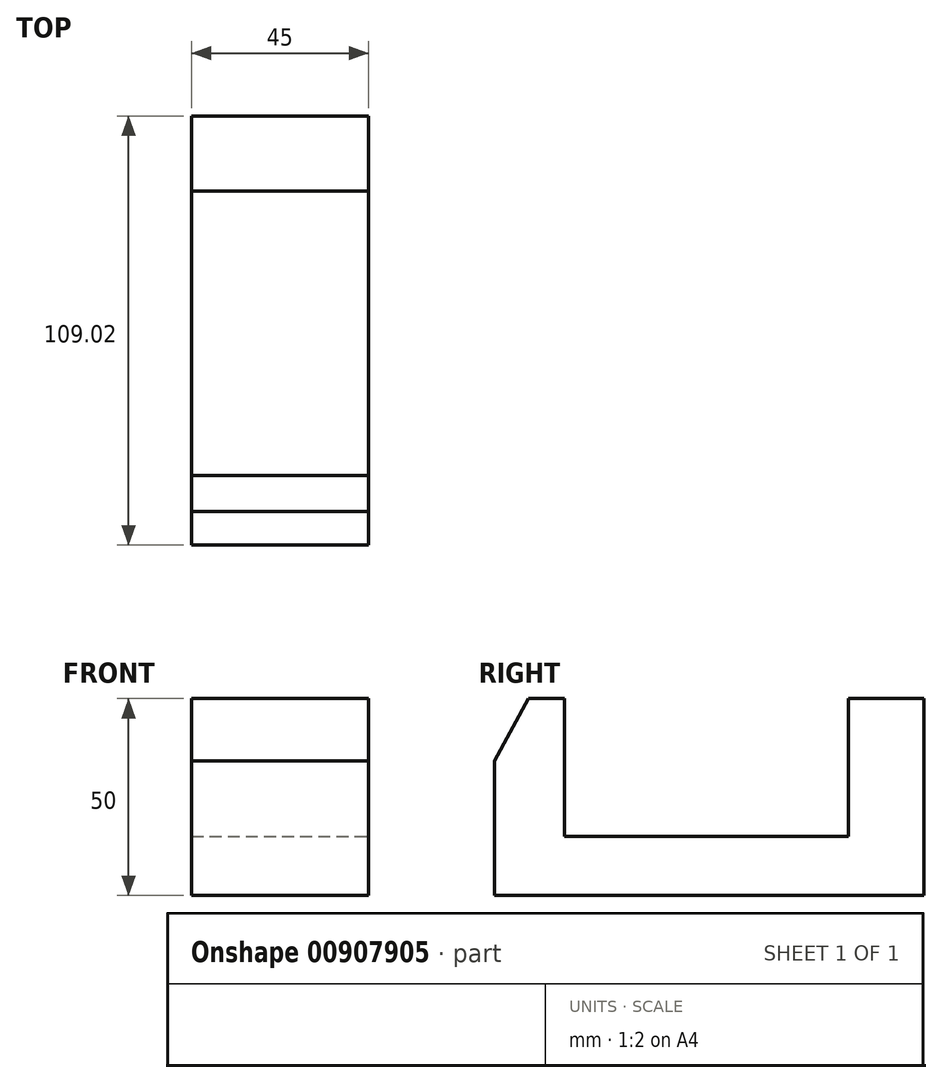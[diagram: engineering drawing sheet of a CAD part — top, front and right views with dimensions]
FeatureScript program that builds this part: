
annotation { "Feature Type Name" : "Feature", "Feature Type Description" : "" }
export const myFeature = defineFeature(function(context is Context, id is Id, definition is map)
    precondition{}
    {
        {
            var Q0;
            Q0=qCreatedBy(makeId("Right.planeOp"),FACE);
            var sketch = newSketch(context, id + "F0", { "sketchPlane" : qUnion([Q0])});
            skLineSegment(sketch, "E0", {"start": v(-51.67, -34.17) * mm, "end": v(57.35, -34.17) * mm});
            skLineSegment(sketch, "E1", {"start": v(-51.67, -34.17) * mm, "end": v(-51.67, 15.83) * mm});
            skLineSegment(sketch, "E2", {"start": v(57.35, -34.17) * mm, "end": v(57.35, 15.83) * mm});
            skLineSegment(sketch, "E3", {"start": v(57.35, 15.83) * mm, "end": v(-51.67, 15.83) * mm});
            skSolve(sketch);
        }
        {
            var Q0;
            Q0=makeQuery(id+"F0.imprint","IMPRINT",FACE,{"disambiguationData":[TD([[makeQuery(id+"F0.imprint","IMPRINT",EDGE,{"derivedFrom":sQuery(id+"F0.wireOp",EDGE,"E0")}),1.0]])]});
            extrude(context, id + "F1", {"entities" : qUnion([Q0]), "depth" : 45 * mm, "offsetDistance" : 25 * mm});
        }
        {
            var Q0;
            Q0=makeQuery(id+"F1.opExtrude","CAP_FACE",FACE,{"disambiguationData":[OSD([sQuery(id+"F0.wireOp",EDGE,"E0"),sQuery(id+"F0.wireOp",EDGE,"E1"),sQuery(id+"F0.wireOp",EDGE,"E2"),sQuery(id+"F0.wireOp",EDGE,"E3")])],"isStart":false});
            var sketch = newSketch(context, id + "F2", { "sketchPlane" : qUnion([Q0])});
            skLineSegment(sketch, "E4", {"start": v(-43.1, 15.83) * mm, "end": v(-51.67, 0) * mm});
            skSolve(sketch);
        }
        {
            var Q0;
            {var subQ0=sQuery(id+"F2.wireOp",EDGE,"E4");Q0=makeQuery(id+"F2.imprint","IMPRINT",FACE,{"disambiguationData":[TD([[makeQuery(id+"F2.imprint","IMPRINT",EDGE,{"derivedFrom":subQ0}),-1.0]])]});}
            extrude(context, id + "F3", {"entities" : qUnion([Q0]), "operationType" : NewBodyOperationType.REMOVE, "oppositeDirection" : true, "depth" : 207 * mm, "offsetDistance" : 25 * mm});
        }
        {
            var Q0;
            Q0=makeQuery(id+"F1.opExtrude","CAP_FACE",FACE,{"disambiguationData":[OSD([sQuery(id+"F0.wireOp",EDGE,"E0"),sQuery(id+"F0.wireOp",EDGE,"E1"),sQuery(id+"F0.wireOp",EDGE,"E2"),sQuery(id+"F0.wireOp",EDGE,"E3")])],"isStart":false});
            var sketch = newSketch(context, id + "F4", { "sketchPlane" : qUnion([Q0])});
            skLineSegment(sketch, "E5", {"start": v(-33.94, 15.83) * mm, "end": v(-33.94, -19.17) * mm});
            skLineSegment(sketch, "E6", {"start": v(-33.94, -19.17) * mm, "end": v(38.23, -19.17) * mm});
            skLineSegment(sketch, "E7", {"start": v(38.23, -19.17) * mm, "end": v(38.23, 15.83) * mm});
            skSolve(sketch);
        }
        {
            var Q0;
            {var subQ0=sQuery(id+"F4.wireOp",EDGE,"E5");Q0=makeQuery(id+"F4.imprint","IMPRINT",FACE,{"disambiguationData":[TD([[makeQuery(id+"F4.imprint","IMPRINT",EDGE,{"derivedFrom":subQ0}),1.0]])]});}
            extrude(context, id + "F5", {"entities" : qUnion([Q0]), "operationType" : NewBodyOperationType.REMOVE, "oppositeDirection" : true, "depth" : 228 * mm, "offsetDistance" : 25 * mm});
        }
    });
